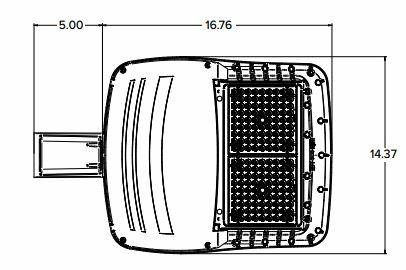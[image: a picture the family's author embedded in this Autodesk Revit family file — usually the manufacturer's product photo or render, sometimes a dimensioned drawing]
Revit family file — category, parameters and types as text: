
# Revit family: VP-1_WM
name_source: partatom
category: Lighting Fixtures
units: mm (PartAtom-declared; Revit-internal decimal feet)

## family parameters
Cut with Voids When Loaded = No
Host = Face
Light Source = No
OmniClass Number = 23.80.70.11.14.17
OmniClass Title = Direct/Indirect
Part Type = Normal
Room Calculation Point = No
Round Connector Dimension = Use Diameter
Shared = Yes

## types (1)
- VP-1-WM
    Apparent Load = 97 VA
    Assembly Code = D5020200
    Brand = Beacon
    CRI = 70
    Certification = UL
    Cool Grey = Cool Grey
    Default Elevation = 48 "
    Description = The Viper is an extremely versatile area/site luminaire which blends design, performance, and technology for a variety of applications.
    Features = Featuring two different optical technologies, Micro Strike and Strike Optics, which provide the best distribution patterns for retrofit or new construction
Vibration rated for high vibration applications including bridges and overpasses
Control options including photo control, occupancy sensing, NX Lighting Controls, wiSCAPE and 7-Pin with networked controls
Mounting options include: Arm, Universal Arm, Adjustable Arm, Mast Arm, Decorative Arm, Knuckle, Trunnion, Wall
Distribution options include: Auto Front Row, Type 2, Type 3, Type 4 Forward, Type 4 Wide, Type 5 Narrow, Type 5 Medium, Type 5 Wide, Type 5 Rectangular, Corner Optic, and Tennis Court
    Finish = Arctic White
    Glass = Glass
    Grey = Grey
    Lamp = LED
    Light Output = 6297 cd/m²
    Load Classification = Lighting
    Manufacturer = Current Lighting
    Matt Black = Matt Black
    Matt Grey = MATT GREY
    Matt White = Matt White
    Model = VP-1-WM
    Name = Viper Area Size 1
    Power Factor = 0.9
    Product Documentation Link = https://cdn.currentlighting.com
    Product Page URL = https://www.currentlighting.com
    Type Comments = Lighting Fixture
    URL = https://www.currentlighting.com
    Voltage = 120 V
    Warranty = Five year warranty
    Wattage Comments = 97.2W

## geometry (parser evidence)
native form markers: Blend x2, Sweep x5
no freeform markers — native parametric forms only
